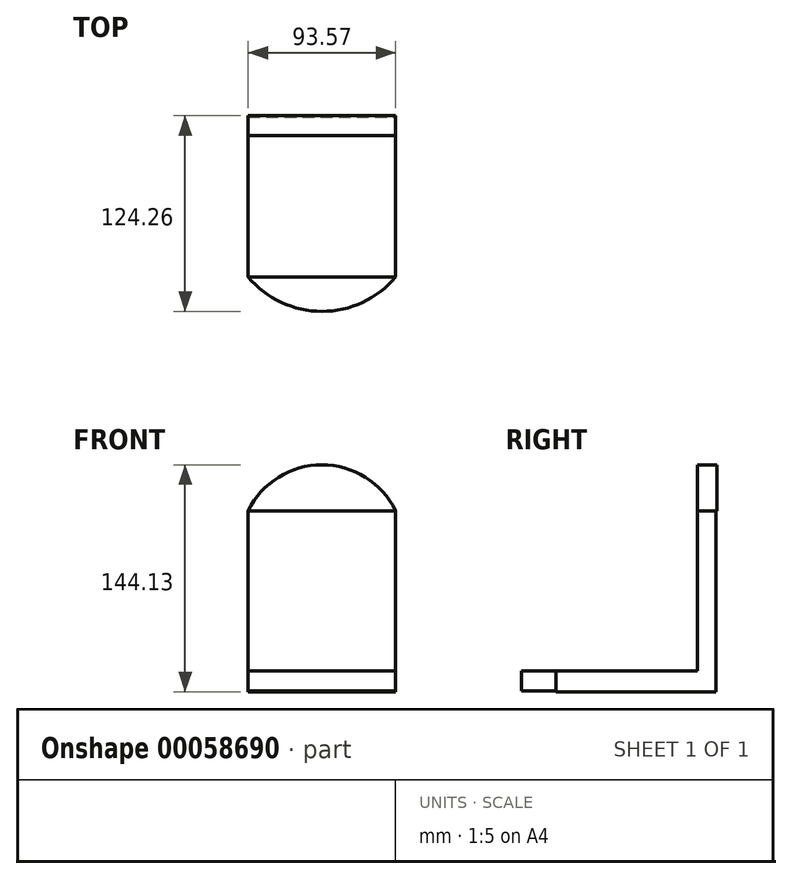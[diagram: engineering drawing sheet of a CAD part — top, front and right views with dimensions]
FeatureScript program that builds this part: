
annotation { "Feature Type Name" : "Feature", "Feature Type Description" : "" }
export const myFeature = defineFeature(function(context is Context, id is Id, definition is map)
    precondition{}
    {
        {
            var Q0;
            Q0=qCreatedBy(makeId("Front.planeOp"),FACE);
            var sketch = newSketch(context, id + "F0", { "sketchPlane" : qUnion([Q0])});
            skLineSegment(sketch, "E0.bottom", {"start": v(-58.4, 9.39) * mm, "end": v(35.16, 9.39) * mm});
            skLineSegment(sketch, "E0.top", {"start": v(-58.4, -4.02) * mm, "end": v(35.16, -4.02) * mm});
            skLineSegment(sketch, "E0.left", {"start": v(-58.4, 9.39) * mm, "end": v(-58.4, -4.02) * mm});
            skLineSegment(sketch, "E0.right", {"start": v(35.16, 9.39) * mm, "end": v(35.16, -4.02) * mm});
            skSolve(sketch);
        }
        {
            var Q0;
            Q0=makeQuery(id+"F0.imprint","IMPRINT",FACE,{"disambiguationData":[TD([[makeQuery(id+"F0.imprint","IMPRINT",EDGE,{"derivedFrom":sQuery(id+"F0.wireOp",EDGE,"E0.bottom")}),-1.0]])]});
            extrude(context, id + "F1", {"entities" : qUnion([Q0]), "depth" : 101.6 * mm});
        }
        {
            var Q0;
            Q0=makeQuery(id+"F1.opExtrude","SWEPT_FACE",FACE,{"disambiguationData":[OSD([sQuery(id+"F0.wireOp",EDGE,"E0.bottom")])]});
            var sketch = newSketch(context, id + "F2", { "sketchPlane" : qUnion([Q0])});
            skLineSegment(sketch, "E1", {"start": v(-58.4, -11.83) * mm, "end": v(35.16, -11.83) * mm});
            skSolve(sketch);
        }
        {
            var Q0;
            {var subQ0=sQuery(id+"F2.wireOp",EDGE,"E1");Q0=makeQuery(id+"F2.imprint","IMPRINT",FACE,{"disambiguationData":[TD([[makeQuery(id+"F2.imprint","IMPRINT",EDGE,{"derivedFrom":subQ0}),1.0]])]});}
            extrude(context, id + "F3", {"entities" : qUnion([Q0]), "operationType" : NewBodyOperationType.ADD, "depth" : 101.6 * mm});
        }
        {
            var Q0;
            Q0=makeQuery(id+"F3.opExtrude","SWEPT_FACE",FACE,{"disambiguationData":[OSD([sQuery(id+"F2.wireOp",EDGE,"E1")])]});
            var sketch = newSketch(context, id + "F4", { "sketchPlane" : qUnion([Q0])});
            skArc(sketch, "E2", {"start": v(35.16, 110.99) * mm, "mid": v(-11.62, 140.1) * mm, "end": v(-58.4, 110.99) * mm});
            skSolve(sketch);
        }
        {
            var Q0;
            Q0=makeQuery(id+"F4.imprint","IMPRINT",FACE,{"disambiguationData":[TD([[makeQuery(id+"F4.imprint","IMPRINT",EDGE,{"derivedFrom":sQuery(id+"F4.wireOp",EDGE,"E2")}),1.0]])]});
            extrude(context, id + "F5", {"entities" : qUnion([Q0]), "oppositeDirection" : true, "depth" : 12.7 * mm});
        }
        {
            var Q0;
            Q0=makeQuery(id+"F1.opExtrude","SWEPT_FACE",FACE,{"disambiguationData":[OSD([sQuery(id+"F0.wireOp",EDGE,"E0.bottom")])]});
            var sketch = newSketch(context, id + "F6", { "sketchPlane" : qUnion([Q0])});
            skArc(sketch, "E3", {"start": v(-58.4, -101.6) * mm, "mid": v(-11.62, -123.39) * mm, "end": v(35.16, -101.6) * mm});
            skSolve(sketch);
        }
        {
            var Q0;
            Q0=makeQuery(id+"F6.imprint","IMPRINT",FACE,{"disambiguationData":[TD([[makeQuery(id+"F6.imprint","IMPRINT",EDGE,{"derivedFrom":sQuery(id+"F6.wireOp",EDGE,"E3")}),1.0]])]});
            extrude(context, id + "F7", {"entities" : qUnion([Q0]), "oppositeDirection" : true, "depth" : 12.7 * mm});
        }
    });
